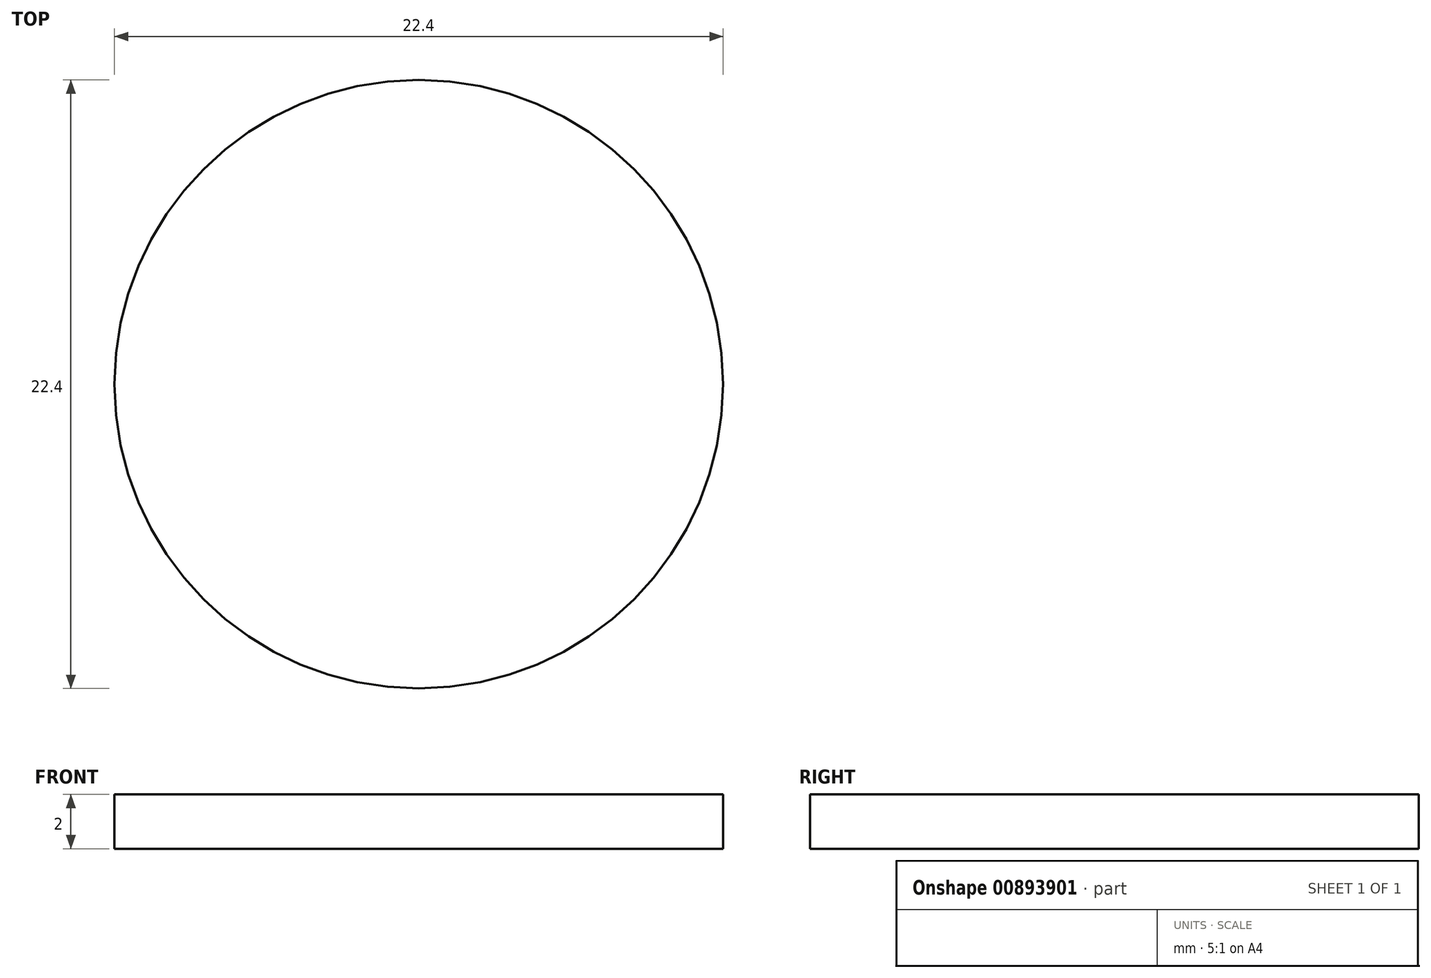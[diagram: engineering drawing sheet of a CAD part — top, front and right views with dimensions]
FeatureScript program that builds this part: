
annotation { "Feature Type Name" : "Feature", "Feature Type Description" : "" }
export const myFeature = defineFeature(function(context is Context, id is Id, definition is map)
    precondition{}
    {
        {
            var Q0;
            Q0=qCreatedBy(makeId("Top.planeOp"),FACE);
            var sketch = newSketch(context, id + "F0", { "sketchPlane" : qUnion([Q0])});
            skCircle(sketch, "E0", {"center": v(0, 0) * mm, "radius": 11.2 * mm});
            skSolve(sketch);
        }
        {
            var Q0;
            Q0 = qSketchRegion(id + "F0", true);
            extrude(context, id + "F1", {"entities" : qUnion([Q0]), "depth" : 2 * mm, "offsetDistance" : 25 * mm});
        }
        {
            var Q0;
            Q0=qCreatedBy(makeId("Top.planeOp"),FACE);
            var sketch = newSketch(context, id + "F2", { "sketchPlane" : qUnion([Q0])});
            skFitSpline(sketch, "E1", {"points": [v(-5.32, 4.11) * mm, v(-4.33, 5.38) * mm, v(-3.78, 6.2) * mm, v(-2.75, 7.16) * mm, v(-1.65, 7.75) * mm, v(0.33, 7.79) * mm, v(1.71, 7.75) * mm, v(3.6, 6.52) * mm, v(4.36, 5.46) * mm, v(5.47, 4.11) * mm, v(4.8, 2.53) * mm, v(5.62, 1.03) * mm, v(5.35, 0.64) * mm, v(4.87, 0.32) * mm, v(4.52, -0.4) * mm, v(4.08, -0.4) * mm, v(3.45, -0.67) * mm, v(2.9, -1.15) * mm], "startDerivative": vector(16.02, 19.31) * mm, "endDerivative": vector(-11.28, -10.7) * mm});
            skFitSpline(sketch, "E2", {"points": [v(-5.32, 4.11) * mm, v(-5.5, 3.89) * mm, v(-5.32, 3.7) * mm, v(-5.02, 3.08) * mm, v(-4.8, 2.6) * mm, v(-4.93, 2.03) * mm, v(-5.32, 1.44) * mm, v(-5.54, 1.03) * mm, v(-5.58, 0.77) * mm, v(-5.32, 0.65) * mm, v(-4.5, -0.42) * mm, v(-4.25, -0.42) * mm, v(-3.42, -0.77) * mm, v(-2.75, -1.42) * mm, v(-2.4, -2.75) * mm, v(-2.06, -3.97) * mm, v(-1.7, -5.1) * mm, v(-1.5, -6.44) * mm, v(0, -7.9) * mm, v(0.6, -7.43) * mm, v(0.52, -7.15) * mm, v(0.62, -7.05) * mm, v(0.94, -7.03) * mm, v(1.02, -6.96) * mm, v(1.53, -6.47) * mm, v(1.53, -6.38) * mm, v(1.61, -5.03) * mm, v(2.12, -3.7) * mm, v(2.12, -3.58) * mm, v(2.66, -1.72) * mm, v(2.58, -0.98) * mm, v(2.64, -0.67) * mm, v(2.9, -1.15) * mm], "startDerivative": vector(-13.14, -11.55) * mm, "endDerivative": vector(10.18, -25.68) * mm});
            skFitSpline(sketch, "E3", {"points": [v(-4.27, 2.02) * mm, v(-4.1, 2.14) * mm, v(-3.6, 2.28) * mm, v(-2.79, 1.86) * mm, v(-1.42, 1.07) * mm, v(-1.22, 1.13) * mm, v(-1.17, 0.9) * mm, v(-1.25, 0.68) * mm, v(-1.28, 0.49) * mm, v(-1.78, 0.32) * mm, v(-2.23, 0.26) * mm, v(-2.35, 0.17) * mm, v(-2.6, 0.16) * mm, v(-3.1, 0.38) * mm, v(-3.65, 0.64) * mm, v(-3.8, 0.82) * mm, v(-4.22, 1.8) * mm, v(-4.27, 2.02) * mm]});
            skFitSpline(sketch, "E4", {"points": [v(1.12, 1.1) * mm, v(1.26, 0.98) * mm, v(1.66, 1.2) * mm, v(3.45, 2.3) * mm, v(3.77, 2.3) * mm, v(4.18, 2.09) * mm, v(4.03, 1.74) * mm, v(3.83, 0.88) * mm, v(3.65, 0.83) * mm, v(3.07, 0.48) * mm, v(2.49, 0.2) * mm, v(2.05, 0.2) * mm, v(1.2, 0.48) * mm, v(1.12, 1.1) * mm]});
            skSolve(sketch);
        }
        {
            var Q0;
            Q0 = qSketchRegion(id + "F2", true);
            extrude(context, id + "F3", {"entities" : qUnion([Q0]), "operationType" : NewBodyOperationType.REMOVE, "oppositeDirection" : true, "depth" : 25 * mm, "offsetDistance" : 25 * mm});
        }
    });
